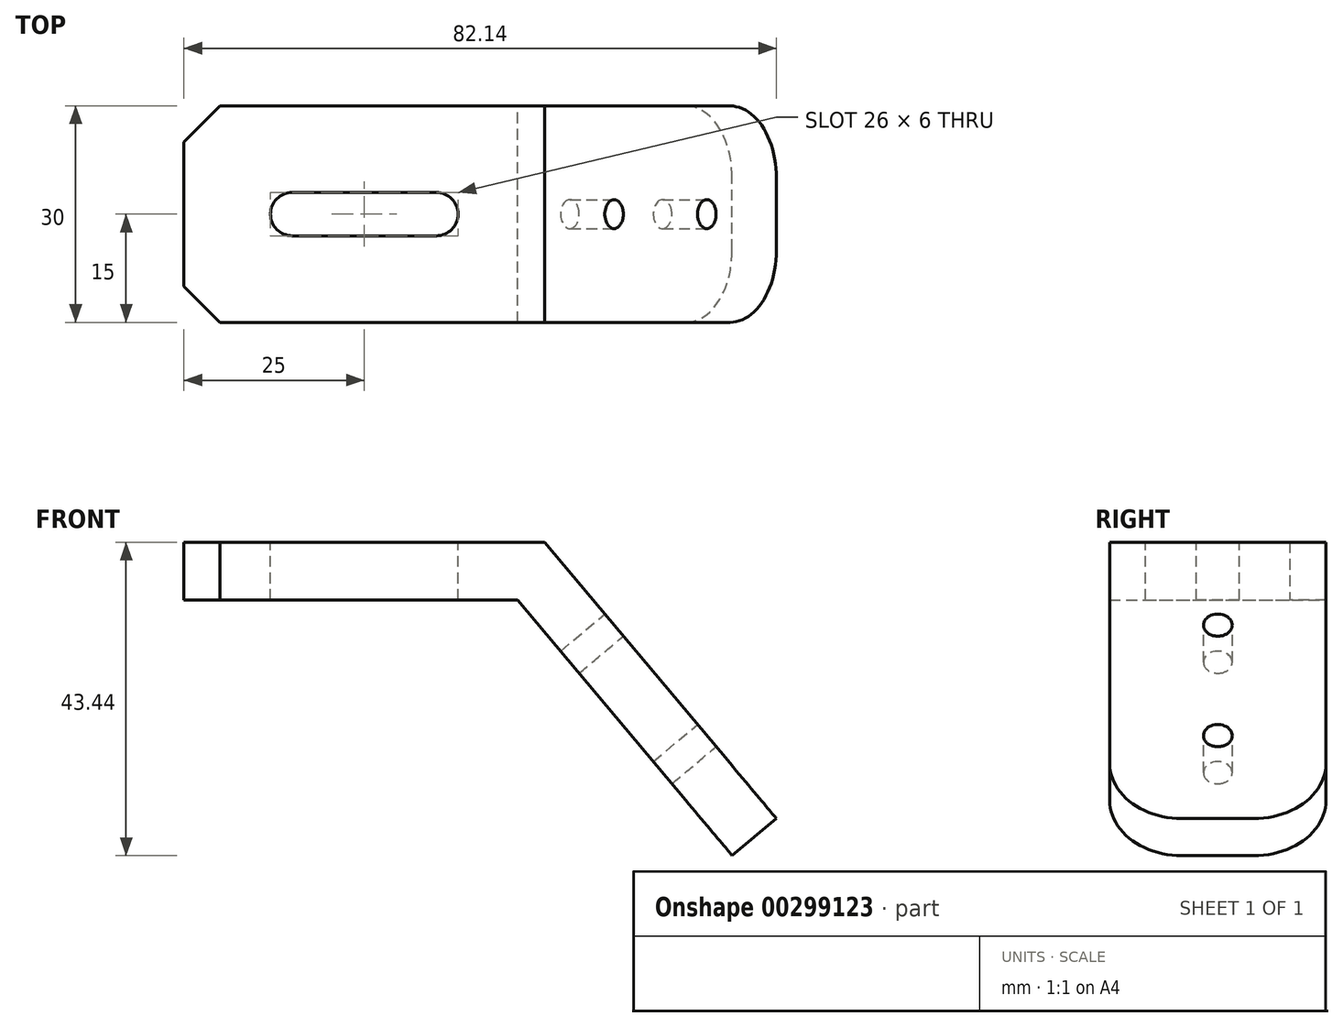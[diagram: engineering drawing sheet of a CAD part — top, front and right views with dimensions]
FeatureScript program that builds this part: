
annotation { "Feature Type Name" : "Feature", "Feature Type Description" : "" }
export const myFeature = defineFeature(function(context is Context, id is Id, definition is map)
    precondition{}
    {
        {
            var Q0;
            Q0=qCreatedBy(makeId("Front.planeOp"),FACE);
            var sketch = newSketch(context, id + "F0", { "sketchPlane" : qUnion([Q0])});
            skLineSegment(sketch, "E0", {"start": v(0, 0) * mm, "end": v(46.27, 0) * mm});
            skLineSegment(sketch, "E1", {"start": v(46.27, 0) * mm, "end": v(76.01, -35.44) * mm});
            skLineSegment(sketch, "E2.0", {"start": v(50, 8) * mm, "end": v(82.14, -30.3) * mm});
            skLineSegment(sketch, "E2.1", {"start": v(0, 8) * mm, "end": v(50, 8) * mm});
            skLineSegment(sketch, "E3", {"start": v(0, 8) * mm, "end": v(0, 0) * mm});
            skLineSegment(sketch, "E4", {"start": v(82.14, -30.3) * mm, "end": v(76.01, -35.44) * mm});
            skSolve(sketch);
        }
        {
            var Q0;
            Q0 = qSketchRegion(id + "F0", true);
            extrude(context, id + "F1", {"entities" : qUnion([Q0]), "endBound" : BoundingType.SYMMETRIC, "depth" : 30 * mm});
        }
        {
            var Q0;
            Q0=makeQuery(id+"F1.opExtrude","SWEPT_FACE",FACE,{"disambiguationData":[OSD([sQuery(id+"F0.wireOp",EDGE,"E2.1")])]});
            var sketch = newSketch(context, id + "F2", { "sketchPlane" : qUnion([Q0])});
            skLineSegment(sketch, "E5", {"start": v(15, 0) * mm, "end": v(35, 0) * mm});
            skArc(sketch, "E6.0.startCap", {"start": v(15, -3) * mm, "mid": v(12, 0) * mm, "end": v(15, 3) * mm});
            skArc(sketch, "E6.0.endCap", {"start": v(35, 3) * mm, "mid": v(38, 0) * mm, "end": v(35, -3) * mm});
            skLineSegment(sketch, "E6.0.left", {"start": v(15, 3) * mm, "end": v(35, 3) * mm});
            skLineSegment(sketch, "E6.0.right", {"start": v(15, -3) * mm, "end": v(35, -3) * mm});
            skSolve(sketch);
        }
        {
            var Q0;
            Q0 = qSketchRegion(id + "F2", true);
            extrude(context, id + "F3", {"entities" : qUnion([Q0]), "operationType" : NewBodyOperationType.REMOVE, "endBound" : BoundingType.THROUGH_ALL, "oppositeDirection" : true, "depth" : 25 * mm});
        }
        {
            var Q0;
            Q0=makeQuery(id+"F1.opExtrude","SWEPT_FACE",FACE,{"disambiguationData":[OSD([sQuery(id+"F0.wireOp",EDGE,"E2.0")])]});
            var sketch = newSketch(context, id + "F4", { "sketchPlane" : qUnion([Q0])});
            skPoint(sketch, "E7", {"position": v(0, -41.01) * mm});
            skPoint(sketch, "E7.positionSnap0", {"position": v(0, -26.01) * mm});
            skPoint(sketch, "E8", {"position": v(0, -61.01) * mm});
            skSolve(sketch);
        }
        {
            var Q0;
            Q0=sQuery(id+"F4.wireOp",VERTEX,"E7");
            var Q1;
            Q1=sQuery(id+"F4.wireOp",VERTEX,"E8");
            var Q2;
            Q2=makeQuery(id+"F1.opExtrude","SWEPT_BODY",BODY,{"disambiguationData":[OSD([sQuery(id+"F0.wireOp",EDGE,"E0"),sQuery(id+"F0.wireOp",EDGE,"E1"),sQuery(id+"F0.wireOp",EDGE,"E2.0"),sQuery(id+"F0.wireOp",EDGE,"E2.1"),sQuery(id+"F0.wireOp",EDGE,"E3"),sQuery(id+"F0.wireOp",EDGE,"E4")])]});
            hole(context, id + "F5", {"style" : HoleStyle.SIMPLE, "endStyle" : HoleEndStyle.THROUGH, "holeDiameter" : 4 * mm, "tappedDepth" : 12 * mm, "tapClearance" : 3, "locations" : qUnion([Q0, Q1]), "scope" : qUnion([Q2])});
        }
        {
            var Q0;
            Q0=makeQuery(id+"F1.opExtrude","CAP_EDGE",EDGE,{"disambiguationData":[OSD([sQuery(id+"F0.wireOp",EDGE,"E4")])],"isStart":false});
            var Q1;
            Q1=makeQuery(id+"F1.opExtrude","CAP_EDGE",EDGE,{"disambiguationData":[OSD([sQuery(id+"F0.wireOp",EDGE,"E4")])],"isStart":true});
            fillet(context, id + "F6", {"entities" : qUnion([Q0, Q1]), "radius" : 10 * mm, "tangentPropagation" : true, "allowEdgeOverflow" : false});
        }
        {
            var Q0;
            Q0=makeQuery(id+"F1.opExtrude","CAP_EDGE",EDGE,{"disambiguationData":[OSD([sQuery(id+"F0.wireOp",EDGE,"E3")])],"isStart":false});
            var Q1;
            Q1=makeQuery(id+"F1.opExtrude","CAP_EDGE",EDGE,{"disambiguationData":[OSD([sQuery(id+"F0.wireOp",EDGE,"E3")])],"isStart":true});
            chamfer(context, id + "F7", {"entities" : qUnion([Q0, Q1]), "width" : 5 * mm, "tangentPropagation" : true});
        }
    });
